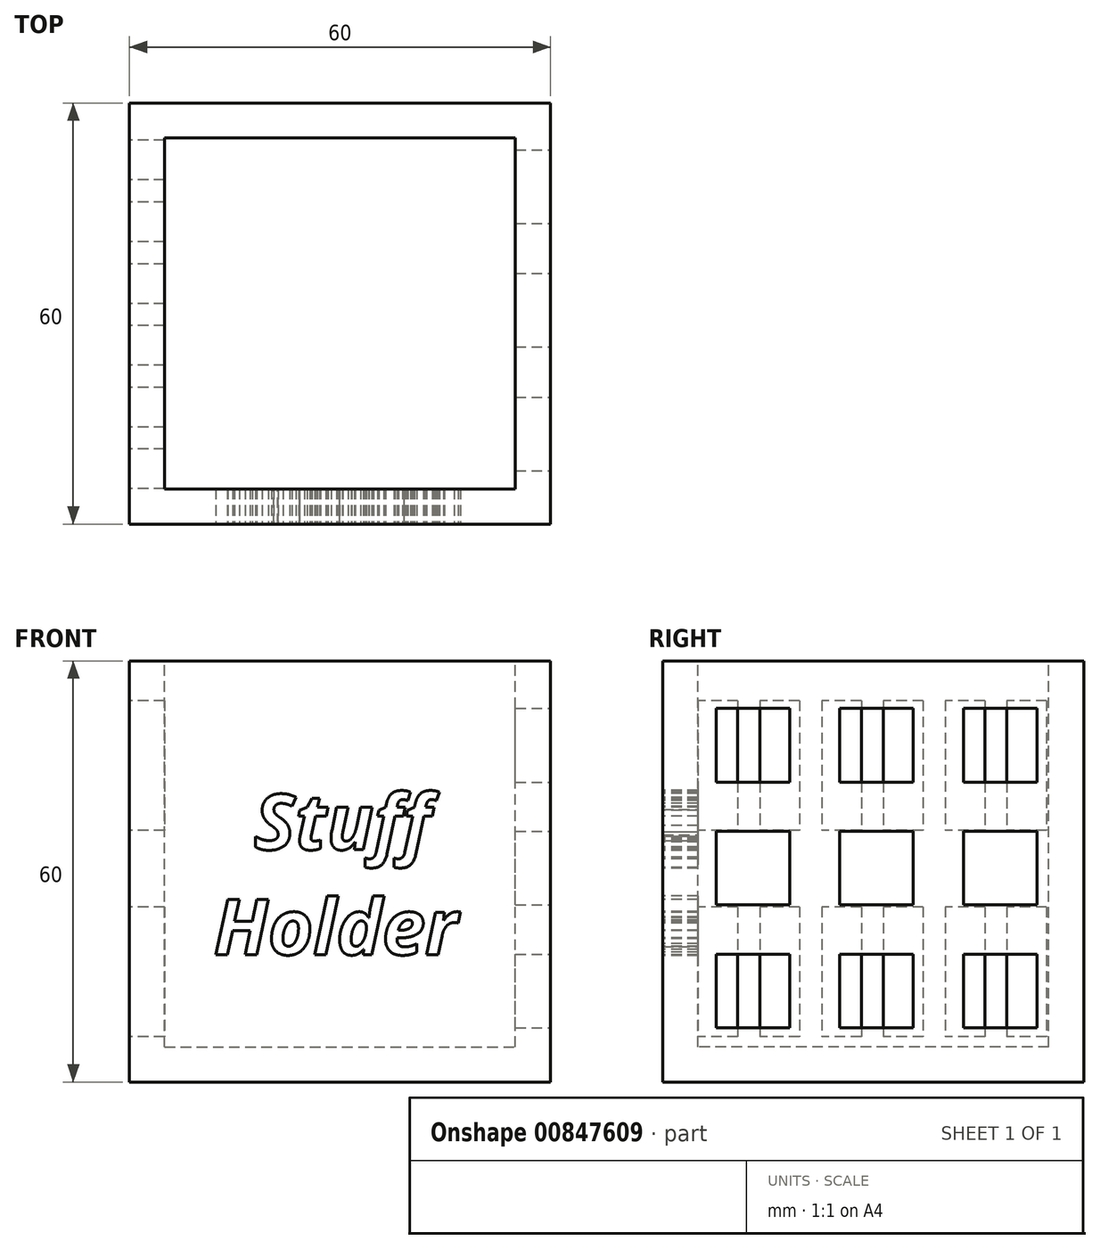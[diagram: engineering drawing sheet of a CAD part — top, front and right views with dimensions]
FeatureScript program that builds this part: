
annotation { "Feature Type Name" : "Feature", "Feature Type Description" : "" }
export const myFeature = defineFeature(function(context is Context, id is Id, definition is map)
    precondition{}
    {
        {
            var Q0;
            Q0=qCreatedBy(makeId("Right.planeOp"),FACE);
            var sketch = newSketch(context, id + "F0", { "sketchPlane" : qUnion([Q0])});
            skLineSegment(sketch, "E0.bottom", {"start": v(-29.86, 29.58) * mm, "end": v(30.14, 29.58) * mm});
            skLineSegment(sketch, "E0.top", {"start": v(-29.86, -30.42) * mm, "end": v(30.14, -30.42) * mm});
            skLineSegment(sketch, "E0.left", {"start": v(-29.86, 29.58) * mm, "end": v(-29.86, -30.42) * mm});
            skLineSegment(sketch, "E0.right", {"start": v(30.14, 29.58) * mm, "end": v(30.14, -30.42) * mm});
            skSolve(sketch);
        }
        {
            var Q0;
            Q0=makeQuery(id+"F0.imprint","IMPRINT",FACE,{"disambiguationData":[TD([[makeQuery(id+"F0.imprint","IMPRINT",EDGE,{"derivedFrom":sQuery(id+"F0.wireOp",EDGE,"E0.bottom")}),-1.0]])]});
            extrude(context, id + "F1", {"entities" : qUnion([Q0]), "depth" : 60 * mm, "offsetDistance" : 25 * mm});
        }
        {
            var Q0;
            Q0=makeQuery(id+"F1.opExtrude","SWEPT_FACE",FACE,{"disambiguationData":[OSD([sQuery(id+"F0.wireOp",EDGE,"E0.bottom")])]});
            var sketch = newSketch(context, id + "F2", { "sketchPlane" : qUnion([Q0])});
            skLineSegment(sketch, "E1.bottom", {"start": v(5, 25.14) * mm, "end": v(55, 25.14) * mm});
            skLineSegment(sketch, "E1.top", {"start": v(5, -24.86) * mm, "end": v(55, -24.86) * mm});
            skLineSegment(sketch, "E1.left", {"start": v(5, 25.14) * mm, "end": v(5, -24.86) * mm});
            skLineSegment(sketch, "E1.right", {"start": v(55, 25.14) * mm, "end": v(55, -24.86) * mm});
            skSolve(sketch);
        }
        {
            var Q0;
            Q0=makeQuery(id+"F2.imprint","IMPRINT",FACE,{"disambiguationData":[TD([[makeQuery(id+"F2.imprint","IMPRINT",EDGE,{"derivedFrom":sQuery(id+"F2.wireOp",EDGE,"E1.bottom")}),-1.0]])]});
            extrude(context, id + "F3", {"entities" : qUnion([Q0]), "operationType" : NewBodyOperationType.REMOVE, "oppositeDirection" : true, "depth" : 55 * mm, "offsetDistance" : 25 * mm});
        }
        {
            var Q0;
            Q0=makeQuery(id+"F1.opExtrude","SWEPT_FACE",FACE,{"disambiguationData":[OSD([sQuery(id+"F0.wireOp",EDGE,"E0.left")])]});
            var sketch = newSketch(context, id + "F4", { "sketchPlane" : qUnion([Q0])});
            skText(sketch, "E2", { "text": "  Stuff\nHolder", "fontName": "OpenSans-BoldItalic.ttf"});
            const initialGuessF4  = {"E2": [0.01204, 0.0027, 1, 0, 0.00793]};
            skSetInitialGuess(sketch, initialGuessF4);
            skSolve(sketch);
        }
        {
            var Q0;
            Q0 = qSketchRegion(id + "F4", true);
            extrude(context, id + "F5", {"entities" : qUnion([Q0]), "operationType" : NewBodyOperationType.REMOVE, "oppositeDirection" : true, "depth" : 10 * mm, "offsetDistance" : 25 * mm});
        }
        {
            var Q0;
            Q0=makeQuery(id+"F1.opExtrude","CAP_FACE",FACE,{"disambiguationData":[OSD([sQuery(id+"F0.wireOp",EDGE,"E0.bottom"),sQuery(id+"F0.wireOp",EDGE,"E0.top"),sQuery(id+"F0.wireOp",EDGE,"E0.left"),sQuery(id+"F0.wireOp",EDGE,"E0.right")])],"isStart":false});
            var sketch = newSketch(context, id + "F6", { "sketchPlane" : qUnion([Q0])});
            skLineSegment(sketch, "E3.bottom", {"start": v(-22.24, 22.8) * mm, "end": v(-11.76, 22.8) * mm});
            skLineSegment(sketch, "E3.top", {"start": v(-22.24, 12.32) * mm, "end": v(-11.76, 12.32) * mm});
            skLineSegment(sketch, "E3.left", {"start": v(-22.24, 22.8) * mm, "end": v(-22.24, 12.32) * mm});
            skLineSegment(sketch, "E3.right", {"start": v(-11.76, 22.8) * mm, "end": v(-11.76, 12.32) * mm});
            skLineSegment(sketch, "E4.0.1.0", {"start": v(-22.24, -5.18) * mm, "end": v(-11.76, -5.18) * mm});
            skLineSegment(sketch, "E4.0.1.1", {"start": v(-22.24, 5.3) * mm, "end": v(-22.24, -5.18) * mm});
            skLineSegment(sketch, "E4.0.1.2", {"start": v(-22.24, 5.3) * mm, "end": v(-11.76, 5.3) * mm});
            skLineSegment(sketch, "E4.0.1.3", {"start": v(-11.76, 5.3) * mm, "end": v(-11.76, -5.18) * mm});
            skLineSegment(sketch, "E4.0.2.0", {"start": v(-22.24, -22.68) * mm, "end": v(-11.76, -22.68) * mm});
            skLineSegment(sketch, "E4.0.2.1", {"start": v(-22.24, -12.2) * mm, "end": v(-22.24, -22.68) * mm});
            skLineSegment(sketch, "E4.0.2.2", {"start": v(-22.24, -12.2) * mm, "end": v(-11.76, -12.2) * mm});
            skLineSegment(sketch, "E4.0.2.3", {"start": v(-11.76, -12.2) * mm, "end": v(-11.76, -22.68) * mm});
            skLineSegment(sketch, "E4.1.0.0", {"start": v(-4.64, 12.32) * mm, "end": v(5.84, 12.32) * mm});
            skLineSegment(sketch, "E4.1.0.1", {"start": v(-4.64, 22.8) * mm, "end": v(-4.64, 12.32) * mm});
            skLineSegment(sketch, "E4.1.0.2", {"start": v(-4.64, 22.8) * mm, "end": v(5.84, 22.8) * mm});
            skLineSegment(sketch, "E4.1.0.3", {"start": v(5.84, 22.8) * mm, "end": v(5.84, 12.32) * mm});
            skLineSegment(sketch, "E4.1.1.0", {"start": v(-4.64, -5.18) * mm, "end": v(5.84, -5.18) * mm});
            skLineSegment(sketch, "E4.1.1.1", {"start": v(-4.64, 5.3) * mm, "end": v(-4.64, -5.18) * mm});
            skLineSegment(sketch, "E4.1.1.2", {"start": v(-4.64, 5.3) * mm, "end": v(5.84, 5.3) * mm});
            skLineSegment(sketch, "E4.1.1.3", {"start": v(5.84, 5.3) * mm, "end": v(5.84, -5.18) * mm});
            skLineSegment(sketch, "E4.1.2.0", {"start": v(-4.64, -22.68) * mm, "end": v(5.84, -22.68) * mm});
            skLineSegment(sketch, "E4.1.2.1", {"start": v(-4.64, -12.2) * mm, "end": v(-4.64, -22.68) * mm});
            skLineSegment(sketch, "E4.1.2.2", {"start": v(-4.64, -12.2) * mm, "end": v(5.84, -12.2) * mm});
            skLineSegment(sketch, "E4.1.2.3", {"start": v(5.84, -12.2) * mm, "end": v(5.84, -22.68) * mm});
            skLineSegment(sketch, "E4.2.0.0", {"start": v(12.96, 12.32) * mm, "end": v(23.44, 12.32) * mm});
            skLineSegment(sketch, "E4.2.0.1", {"start": v(12.96, 22.8) * mm, "end": v(12.96, 12.32) * mm});
            skLineSegment(sketch, "E4.2.0.2", {"start": v(12.96, 22.8) * mm, "end": v(23.44, 22.8) * mm});
            skLineSegment(sketch, "E4.2.0.3", {"start": v(23.44, 22.8) * mm, "end": v(23.44, 12.32) * mm});
            skLineSegment(sketch, "E4.2.1.0", {"start": v(12.96, -5.18) * mm, "end": v(23.44, -5.18) * mm});
            skLineSegment(sketch, "E4.2.1.1", {"start": v(12.96, 5.3) * mm, "end": v(12.96, -5.18) * mm});
            skLineSegment(sketch, "E4.2.1.2", {"start": v(12.96, 5.3) * mm, "end": v(23.44, 5.3) * mm});
            skLineSegment(sketch, "E4.2.1.3", {"start": v(23.44, 5.3) * mm, "end": v(23.44, -5.18) * mm});
            skLineSegment(sketch, "E4.2.2.0", {"start": v(12.96, -22.68) * mm, "end": v(23.44, -22.68) * mm});
            skLineSegment(sketch, "E4.2.2.1", {"start": v(12.96, -12.2) * mm, "end": v(12.96, -22.68) * mm});
            skLineSegment(sketch, "E4.2.2.2", {"start": v(12.96, -12.2) * mm, "end": v(23.44, -12.2) * mm});
            skLineSegment(sketch, "E4.2.2.3", {"start": v(23.44, -12.2) * mm, "end": v(23.44, -22.68) * mm});
            skLineSegment(sketch, "E4.direction1", {"start": v(-22.24, 12.32) * mm, "end": v(-4.64, 12.32) * mm, "construction": true});
            skLineSegment(sketch, "E4.direction2", {"start": v(-22.24, 12.32) * mm, "end": v(-22.24, -5.18) * mm, "construction": true});
            skSolve(sketch);
        }
        {
            var Q0;
            Q0 = qSketchRegion(id + "F6", true);
            extrude(context, id + "F7", {"entities" : qUnion([Q0]), "operationType" : NewBodyOperationType.REMOVE, "oppositeDirection" : true, "depth" : 10 * mm, "offsetDistance" : 25 * mm});
        }
        {
            var Q0;
            Q0=makeQuery(id+"F1.opExtrude","CAP_FACE",FACE,{"disambiguationData":[OSD([sQuery(id+"F0.wireOp",EDGE,"E0.bottom"),sQuery(id+"F0.wireOp",EDGE,"E0.top"),sQuery(id+"F0.wireOp",EDGE,"E0.left"),sQuery(id+"F0.wireOp",EDGE,"E0.right")])],"isStart":true});
            var sketch = newSketch(context, id + "F8", { "sketchPlane" : qUnion([Q0])});
            skLineSegment(sketch, "E5.bottom", {"start": v(-24.82, 23.94) * mm, "end": v(-19.18, 23.94) * mm});
            skLineSegment(sketch, "E5.top", {"start": v(-24.82, 5.46) * mm, "end": v(-19.18, 5.46) * mm});
            skLineSegment(sketch, "E5.left", {"start": v(-24.82, 23.94) * mm, "end": v(-24.82, 5.46) * mm});
            skLineSegment(sketch, "E5.right", {"start": v(-19.18, 23.94) * mm, "end": v(-19.18, 5.46) * mm});
            skLineSegment(sketch, "E6.0.1.0", {"start": v(-24.82, -5.46) * mm, "end": v(-19.18, -5.46) * mm});
            skLineSegment(sketch, "E6.0.1.1", {"start": v(-19.18, -5.46) * mm, "end": v(-19.18, -23.94) * mm});
            skLineSegment(sketch, "E6.0.1.2", {"start": v(-24.82, -5.46) * mm, "end": v(-24.82, -23.94) * mm});
            skLineSegment(sketch, "E6.0.1.3", {"start": v(-24.82, -23.94) * mm, "end": v(-19.18, -23.94) * mm});
            skLineSegment(sketch, "E6.1.0.0", {"start": v(-16.02, 23.94) * mm, "end": v(-10.38, 23.94) * mm});
            skLineSegment(sketch, "E6.1.0.1", {"start": v(-10.38, 23.94) * mm, "end": v(-10.38, 5.46) * mm});
            skLineSegment(sketch, "E6.1.0.2", {"start": v(-16.02, 23.94) * mm, "end": v(-16.02, 5.46) * mm});
            skLineSegment(sketch, "E6.1.0.3", {"start": v(-16.02, 5.46) * mm, "end": v(-10.38, 5.46) * mm});
            skLineSegment(sketch, "E6.1.1.0", {"start": v(-16.02, -5.46) * mm, "end": v(-10.38, -5.46) * mm});
            skLineSegment(sketch, "E6.1.1.1", {"start": v(-10.38, -5.46) * mm, "end": v(-10.38, -23.94) * mm});
            skLineSegment(sketch, "E6.1.1.2", {"start": v(-16.02, -5.46) * mm, "end": v(-16.02, -23.94) * mm});
            skLineSegment(sketch, "E6.1.1.3", {"start": v(-16.02, -23.94) * mm, "end": v(-10.38, -23.94) * mm});
            skLineSegment(sketch, "E6.2.0.0", {"start": v(-7.22, 23.94) * mm, "end": v(-1.58, 23.94) * mm});
            skLineSegment(sketch, "E6.2.0.1", {"start": v(-1.58, 23.94) * mm, "end": v(-1.58, 5.46) * mm});
            skLineSegment(sketch, "E6.2.0.2", {"start": v(-7.22, 23.94) * mm, "end": v(-7.22, 5.46) * mm});
            skLineSegment(sketch, "E6.2.0.3", {"start": v(-7.22, 5.46) * mm, "end": v(-1.58, 5.46) * mm});
            skLineSegment(sketch, "E6.2.1.0", {"start": v(-7.22, -5.46) * mm, "end": v(-1.58, -5.46) * mm});
            skLineSegment(sketch, "E6.2.1.1", {"start": v(-1.58, -5.46) * mm, "end": v(-1.58, -23.94) * mm});
            skLineSegment(sketch, "E6.2.1.2", {"start": v(-7.22, -5.46) * mm, "end": v(-7.22, -23.94) * mm});
            skLineSegment(sketch, "E6.2.1.3", {"start": v(-7.22, -23.94) * mm, "end": v(-1.58, -23.94) * mm});
            skLineSegment(sketch, "E6.3.0.0", {"start": v(1.58, 23.94) * mm, "end": v(7.22, 23.94) * mm});
            skLineSegment(sketch, "E6.3.0.1", {"start": v(7.22, 23.94) * mm, "end": v(7.22, 5.46) * mm});
            skLineSegment(sketch, "E6.3.0.2", {"start": v(1.58, 23.94) * mm, "end": v(1.58, 5.46) * mm});
            skLineSegment(sketch, "E6.3.0.3", {"start": v(1.58, 5.46) * mm, "end": v(7.22, 5.46) * mm});
            skLineSegment(sketch, "E6.3.1.0", {"start": v(1.58, -5.46) * mm, "end": v(7.22, -5.46) * mm});
            skLineSegment(sketch, "E6.3.1.1", {"start": v(7.22, -5.46) * mm, "end": v(7.22, -23.94) * mm});
            skLineSegment(sketch, "E6.3.1.2", {"start": v(1.58, -5.46) * mm, "end": v(1.58, -23.94) * mm});
            skLineSegment(sketch, "E6.3.1.3", {"start": v(1.58, -23.94) * mm, "end": v(7.22, -23.94) * mm});
            skLineSegment(sketch, "E6.4.0.0", {"start": v(10.38, 23.94) * mm, "end": v(16.02, 23.94) * mm});
            skLineSegment(sketch, "E6.4.0.1", {"start": v(16.02, 23.94) * mm, "end": v(16.02, 5.46) * mm});
            skLineSegment(sketch, "E6.4.0.2", {"start": v(10.38, 23.94) * mm, "end": v(10.38, 5.46) * mm});
            skLineSegment(sketch, "E6.4.0.3", {"start": v(10.38, 5.46) * mm, "end": v(16.02, 5.46) * mm});
            skLineSegment(sketch, "E6.4.1.0", {"start": v(10.38, -5.46) * mm, "end": v(16.02, -5.46) * mm});
            skLineSegment(sketch, "E6.4.1.1", {"start": v(16.02, -5.46) * mm, "end": v(16.02, -23.94) * mm});
            skLineSegment(sketch, "E6.4.1.2", {"start": v(10.38, -5.46) * mm, "end": v(10.38, -23.94) * mm});
            skLineSegment(sketch, "E6.4.1.3", {"start": v(10.38, -23.94) * mm, "end": v(16.02, -23.94) * mm});
            skLineSegment(sketch, "E6.5.0.0", {"start": v(19.18, 23.94) * mm, "end": v(24.82, 23.94) * mm});
            skLineSegment(sketch, "E6.5.0.1", {"start": v(24.82, 23.94) * mm, "end": v(24.82, 5.46) * mm});
            skLineSegment(sketch, "E6.5.0.2", {"start": v(19.18, 23.94) * mm, "end": v(19.18, 5.46) * mm});
            skLineSegment(sketch, "E6.5.0.3", {"start": v(19.18, 5.46) * mm, "end": v(24.82, 5.46) * mm});
            skLineSegment(sketch, "E6.5.1.0", {"start": v(19.18, -5.46) * mm, "end": v(24.82, -5.46) * mm});
            skLineSegment(sketch, "E6.5.1.1", {"start": v(24.82, -5.46) * mm, "end": v(24.82, -23.94) * mm});
            skLineSegment(sketch, "E6.5.1.2", {"start": v(19.18, -5.46) * mm, "end": v(19.18, -23.94) * mm});
            skLineSegment(sketch, "E6.5.1.3", {"start": v(19.18, -23.94) * mm, "end": v(24.82, -23.94) * mm});
            skLineSegment(sketch, "E6.direction1", {"start": v(-24.82, 23.94) * mm, "end": v(-16.02, 23.94) * mm, "construction": true});
            skLineSegment(sketch, "E6.direction2", {"start": v(-24.82, 23.94) * mm, "end": v(-24.82, -5.46) * mm, "construction": true});
            skSolve(sketch);
        }
        {
            var Q0;
            Q0 = qSketchRegion(id + "F8", true);
            extrude(context, id + "F9", {"entities" : qUnion([Q0]), "operationType" : NewBodyOperationType.REMOVE, "oppositeDirection" : true, "depth" : 10 * mm, "offsetDistance" : 25 * mm});
        }
    });
